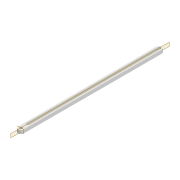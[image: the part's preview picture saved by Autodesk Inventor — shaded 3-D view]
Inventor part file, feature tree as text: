
AUTODESK INVENTOR PART (.ipt)
format: ipt  version: 2022 (Build 260153000, 153)  size: 90,624 bytes
history: native  units: mm
features: extrude x1, sketch x1
ambient origin geometry x8: Origin, YZ Plane, XZ Plane, XY Plane, X Axis, Y Axis, Z Axis, Center Point
bodies: Solid1 (feature_tree)
feature tree (2):
  extrude  "Extrusion1"  Depth=200.0mm
  sketch  "Sketch1"  dims[d0=8.0mm d1=200.0mm d2=4.2mm d3=4.2mm d4=10.0mm d5=5.0mm d6=0.0mm]
